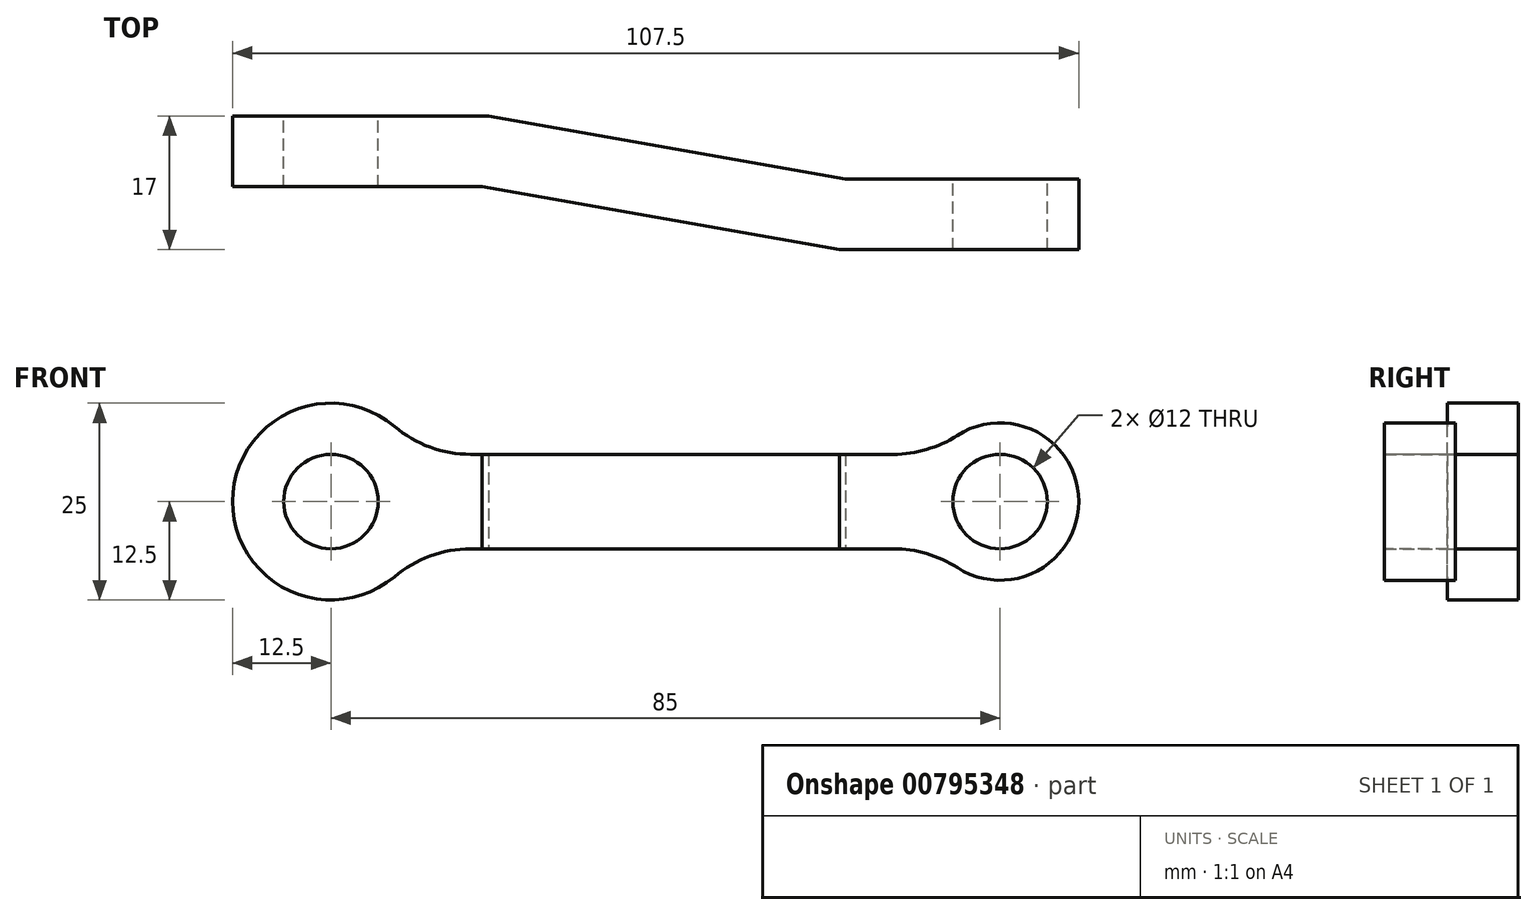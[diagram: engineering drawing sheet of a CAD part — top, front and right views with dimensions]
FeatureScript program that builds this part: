
annotation { "Feature Type Name" : "Feature", "Feature Type Description" : "" }
export const myFeature = defineFeature(function(context is Context, id is Id, definition is map)
    precondition{}
    {
        {
            var Q0;
            Q0=qCreatedBy(makeId("Front.planeOp"),FACE);
            var sketch = newSketch(context, id + "F0", { "sketchPlane" : qUnion([Q0])});
            skCircle(sketch, "E0", {"center": v(0, 0) * mm, "radius": 12.5 * mm});
            skCircle(sketch, "E1", {"center": v(85, 0) * mm, "radius": 10 * mm});
            skLineSegment(sketch, "E2", {"start": v(0, 0) * mm, "end": v(85, 0) * mm, "construction": true});
            skLineSegment(sketch, "E3", {"start": v(77, 6) * mm, "end": v(10.97, 6) * mm});
            skLineSegment(sketch, "E4.MirrorCS", {"start": v(77, -6) * mm, "end": v(10.97, -6) * mm});
            skCircle(sketch, "E5", {"center": v(0, 0) * mm, "radius": 6 * mm});
            skCircle(sketch, "E6", {"center": v(85, 0) * mm, "radius": 6 * mm});
            skSolve(sketch);
        }
        {
            var Q0;
            Q0 = qSketchRegion(id + "F0", true);
            extrude(context, id + "F1", {"entities" : qUnion([Q0]), "depth" : 25 * mm, "offsetDistance" : 25 * mm});
        }
        {
            var Q0;
            Q0=qCreatedBy(makeId("Top.planeOp"),FACE);
            var sketch = newSketch(context, id + "F2", { "sketchPlane" : qUnion([Q0])});
            skLineSegment(sketch, "E7", {"start": v(-12.5, 0) * mm, "end": v(0, 0) * mm});
            skLineSegment(sketch, "E8", {"start": v(0, 0) * mm, "end": v(20, 0) * mm});
            skLineSegment(sketch, "E9", {"start": v(20, 0) * mm, "end": v(65.37, -8) * mm});
            skLineSegment(sketch, "E10", {"start": v(65.37, -8) * mm, "end": v(95, -8) * mm});
            skLineSegment(sketch, "E11.0", {"start": v(64.58, -17) * mm, "end": v(95, -17) * mm});
            skLineSegment(sketch, "E11.1", {"start": v(19.21, -9) * mm, "end": v(64.58, -17) * mm});
            skLineSegment(sketch, "E11.2", {"start": v(0, -9) * mm, "end": v(19.21, -9) * mm});
            skLineSegment(sketch, "E11.3", {"start": v(-12.5, -9) * mm, "end": v(0, -9) * mm});
            skLineSegment(sketch, "E12", {"start": v(-12.5, -9) * mm, "end": v(-12.5, 0) * mm});
            skLineSegment(sketch, "E13", {"start": v(95, -17) * mm, "end": v(95, -8) * mm});
            skLineSegment(sketch, "E14", {"start": v(-12.5, -25) * mm, "end": v(-12.5, 0) * mm});
            skLineSegment(sketch, "E15", {"start": v(95, 0) * mm, "end": v(95, -25) * mm});
            skSolve(sketch);
        }
        {
            var Q0;
            Q0 = qSketchRegion(id + "F2", true);
            extrude(context, id + "F3", {"entities" : qUnion([Q0]), "operationType" : NewBodyOperationType.INTERSECT, "endBound" : BoundingType.SYMMETRIC, "depth" : 25 * mm, "offsetDistance" : 25 * mm});
        }
        {
            var Q0;
            Q0=makeQuery(id+"F1.opExtrude","SWEPT_EDGE",EDGE,{"disambiguationData":[OSD([sQuery(id+"F0.wireOp",EDGE,"E0"),sQuery(id+"F0.wireOp",EDGE,"E4.MirrorCS")])]});
            var Q1;
            Q1=makeQuery(id+"F1.opExtrude","SWEPT_EDGE",EDGE,{"disambiguationData":[OSD([sQuery(id+"F0.wireOp",EDGE,"E0"),sQuery(id+"F0.wireOp",EDGE,"E3")])]});
            var Q2;
            Q2=makeQuery(id+"F1.opExtrude","SWEPT_EDGE",EDGE,{"disambiguationData":[OSD([sQuery(id+"F0.wireOp",EDGE,"E1"),sQuery(id+"F0.wireOp",EDGE,"E3")])]});
            var Q3;
            Q3=makeQuery(id+"F1.opExtrude","SWEPT_EDGE",EDGE,{"disambiguationData":[OSD([sQuery(id+"F0.wireOp",EDGE,"E1"),sQuery(id+"F0.wireOp",EDGE,"E4.MirrorCS")])]});
            fillet(context, id + "F4", {"entities" : qUnion([Q0, Q1, Q2, Q3]), "radius" : 15 * mm, "tangentPropagation" : true, "allowEdgeOverflow" : false});
        }
    });
